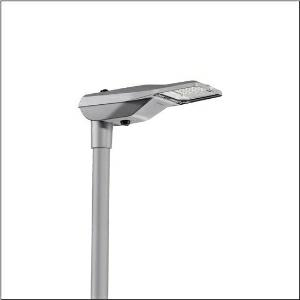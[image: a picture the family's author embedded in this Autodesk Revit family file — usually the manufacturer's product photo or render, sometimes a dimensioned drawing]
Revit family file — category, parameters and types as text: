
# Revit family: streetlight_sl_21_iq_micro___st1_0a_5xe1d21y08db_e1fc
name_source: partatom
category: Lighting Fixtures
units: mm (PartAtom-declared; Revit-internal decimal feet)

## family parameters
Cut with Voids When Loaded = No
Host = Face
Light Source = No
Part Type = Normal
Room Calculation Point = No
Round Connector Dimension = Use Diameter
Shared = No

## types (1)
- --- (1 x LED, 4100 lm, 39.1 W, 2200K)
    Apparent Load = 39 VA
    CIE Flux Codes = 37 72 97 100 100
    Color Rendering = 70
    Color Temperature = 2200K
    Default Elevation = 1800 mm
    Description = Streetlight SL 21 iQ micro, mast luminaire, primary light control with lens, of PMMA, primary optical cover: cover, of toughened safety glass, transparent, light distribution: ST1.0a, light emission: direct distribution, primary light characteristic: asymmetric, installation type: post-top, side-entry, LED, High Power LED, rated luminous flux: 4.100lm, luminous efficacy: 105lm/W, light colour: 722, colour temperature: 2200K, control gear: iQ-Street Remote, D4i with power reduction, control: pre-setting: logarithmic dimming characteristic, Street-Remote, Auto-Match, Temp-Guard, Lumen-Switch, Night-Set, Smart-Wire, Light-Fading, Desk-Remote (wireless, voltage-free reading and setting of iQ features in the workshop via application-optimized NFC function/RFID function), optimised constant luminous flux control (CLO 2.0), mains connection: 220..240V, AC, 50/60Hz, start of lifetime: 39W, end of service life: 41W, reduction: 17W, luminaire housing, of diecast aluminium, powder-coated, Siteco® metallic grey (DB 702S), corrosivity category C5 mid according to DIN EN ISO 12944, please order mast flange separately, inclination adjustable: 0°, 5°, 10°, 15°, sealing non-destructively replaceable, multi-level sealing system, length: 528mm, width: 235mm, height: 110mm, mast flange for spigot size: 42mm (side-entry): 5XC10008XM4, 60/48mm (side-entry/post-top): 5XC10108XM2, 76/60mm (side-entry/post-top): 5XC10108XM1, mounting height: 4..8m, Smart Interface below and above, protection rating (complete): IP66, insulation class (complete): insulation class II (safety insulation), certification: CE, ENEC, ENEC+, VDE, impact resistance: IK10, permissible operating ambient temperature for outdoor applications: -40..+50°C, standard-compliant lighting for roads and squares, packaging unit: 1 piece

Light Distribution: ST1.0a
    Height = 110 mm
    Lamp = 1 x LED
    Lamp Light Flux = 4100 lm
    Lamp Power = 39.1 W
    Lamp count = 1
    Length = 528 mm
    Luminous efficacy = 105 lm/W
    Manufacturer = Siteco
    ModVariant = No
    Model = 5XE1D21Y08DB
    Number of Poles = 1
    OnlyDefault = Yes
    Power Factor = 1
    Product Name = Streetlight SL 21 iQ micro | ST1.0a
    Product group = mast luminaire | pylon top
    ProductGroupID = 6100
    Protection Class = Protection class II
    Protection Degree = IP 66
    RLX_Detail_Level = 1
    RLX_Emergency_Light_Flux = 0 lm
    RLX_Emergency_Type = 0
    RLX_Emergency_Type_DB = No
    RlxData = <blob elided: 98685 chars, md5=361cdece>
    Socket = socket
    Standby Power = 0 W
    System Light Flux = 4100 lm
    System Power = 39 W
    Type Comments = factory setting: luminous flux: 100 % | dim-lin: 254 | 765 mA
    Type Image = l_1007239.jpg
    URL = http://relux.com
    VarID = @adj_115570
    Voltage = 0 V
    Weight = 0.00 kg
    Width = 235 mm

## geometry (parser evidence)
native form markers: Blend x4, Sweep x10
no freeform markers — native parametric forms only
